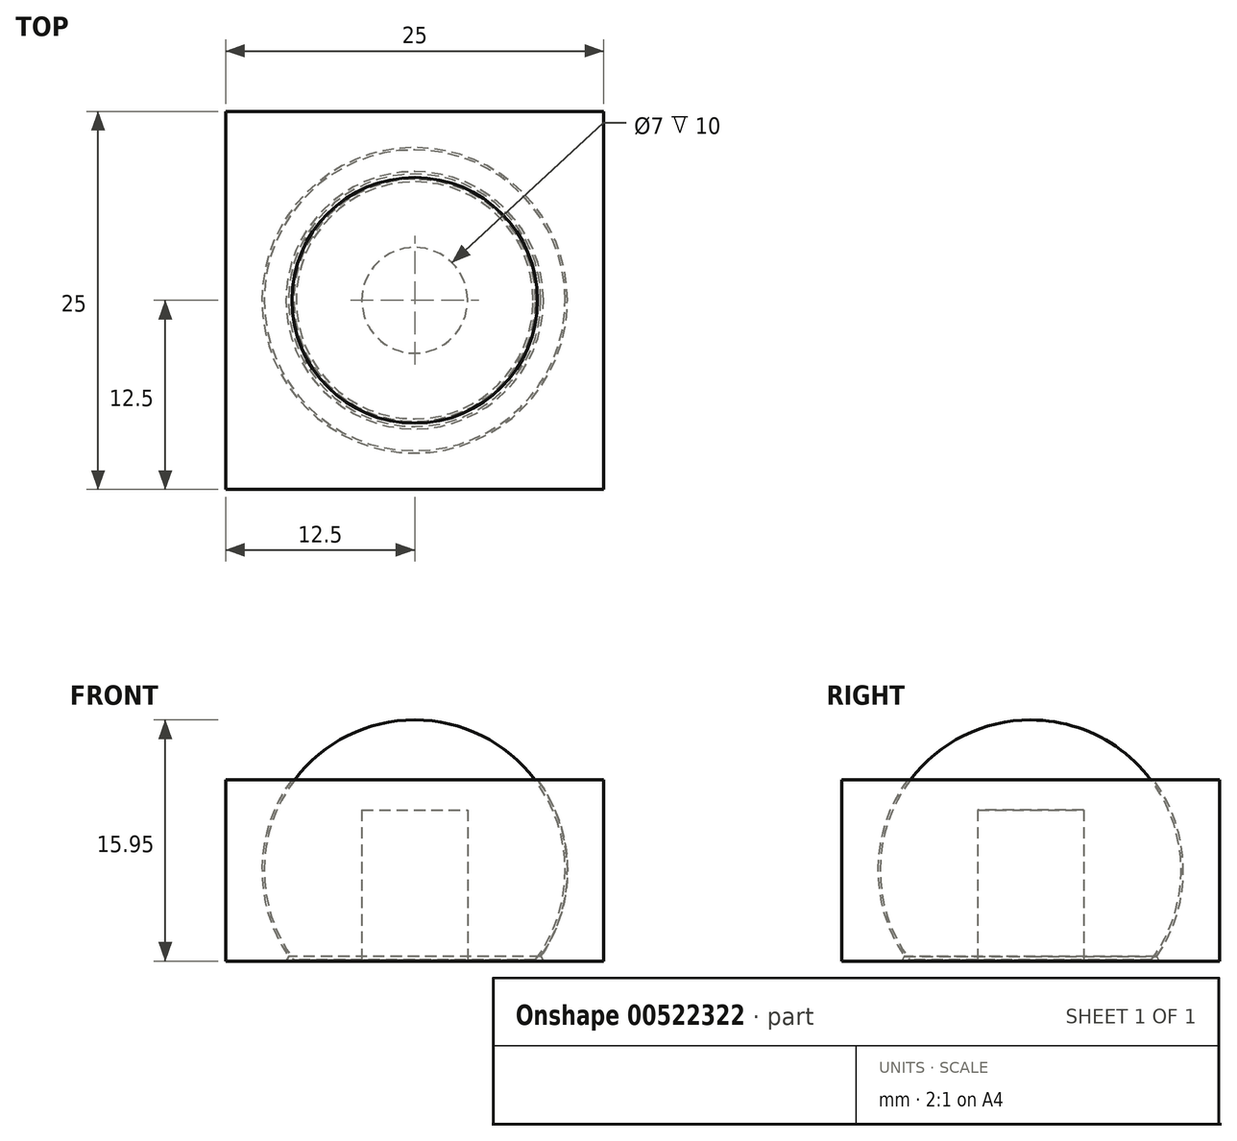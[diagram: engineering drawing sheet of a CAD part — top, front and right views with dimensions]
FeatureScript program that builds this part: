
annotation { "Feature Type Name" : "Feature", "Feature Type Description" : "" }
export const myFeature = defineFeature(function(context is Context, id is Id, definition is map)
    precondition{}
    {
        {
            var Q0;
            Q0=qCreatedBy(makeId("Top.planeOp"),FACE);
            var sketch = newSketch(context, id + "F0", { "sketchPlane" : qUnion([Q0])});
            skLineSegment(sketch, "E0.bottom", {"start": v(-12.5, 12.5) * mm, "end": v(12.5, 12.5) * mm});
            skLineSegment(sketch, "E0.top", {"start": v(-12.5, -12.5) * mm, "end": v(12.5, -12.5) * mm});
            skLineSegment(sketch, "E0.left", {"start": v(-12.5, 12.5) * mm, "end": v(-12.5, -12.5) * mm});
            skLineSegment(sketch, "E0.right", {"start": v(12.5, 12.5) * mm, "end": v(12.5, -12.5) * mm});
            skLineSegment(sketch, "E1", {"start": v(0, -17.22) * mm, "end": v(0, 15.83) * mm, "construction": true});
            skLineSegment(sketch, "E2", {"start": v(-20.04, 0) * mm, "end": v(21, 0) * mm, "construction": true});
            skSolve(sketch);
        }
        {
            var Q0;
            Q0 = qSketchRegion(id + "F0", true);
            extrude(context, id + "F1", {"entities" : qUnion([Q0]), "depth" : 12 * mm, "offsetDistance" : 25 * mm});
        }
        {
            var Q0;
            Q0=qCreatedBy(makeId("Right.planeOp"),FACE);
            var sketch = newSketch(context, id + "F2", { "sketchPlane" : qUnion([Q0])});
            skLineSegment(sketch, "E3.0", {"start": v(12.5, 0) * mm, "end": v(-12.5, 0) * mm, "construction": true});
            skLineSegment(sketch, "E3.1", {"start": v(12.5, 12) * mm, "end": v(-12.5, 12) * mm, "construction": true});
            skLineSegment(sketch, "E4", {"start": v(-21.21, 6) * mm, "end": v(21.87, 6) * mm, "construction": true});
            skArc(sketch, "E5", {"start": v(0, -4.1) * mm, "mid": v(10.1, 6) * mm, "end": v(0, 16.1) * mm});
            skLineSegment(sketch, "E6", {"start": v(0, 16.1) * mm, "end": v(0, -4.1) * mm});
            skSolve(sketch);
        }
        {
            var Q0;
            Q0=makeQuery(id+"F2.imprint","IMPRINT",FACE,{"disambiguationData":[TD([[makeQuery(id+"F2.imprint","IMPRINT",EDGE,{"derivedFrom":sQuery(id+"F2.wireOp",EDGE,"E5")}),1.0]])]});
            var Q1;
            Q1=sQuery(id+"F2.wireOp",EDGE,"E5");
            var Q2;
            Q2=sQuery(id+"F2.wireOp",EDGE,"E6");
            revolve(context, id + "F3", {"operationType" : NewBodyOperationType.REMOVE, "entities" : qUnion([Q0]), "surfaceEntities" : qUnion([Q1]), "axis" : qUnion([Q2]), "revolveType" : RevolveType.FULL, "oppositeDirection" : true});
        }
        {
            var Q0;
            Q0=qCreatedBy(makeId("Right.planeOp"),FACE);
            var sketch = newSketch(context, id + "F4", { "sketchPlane" : qUnion([Q0])});
            skArc(sketch, "E7.0", {"start": v(0, -4.1) * mm, "mid": v(10.1, 6) * mm, "end": v(0, 16.1) * mm, "construction": true});
            skLineSegment(sketch, "E7.1", {"start": v(0, 16.1) * mm, "end": v(0, 0) * mm, "construction": true});
            skArc(sketch, "E8", {"start": v(7.94, 0) * mm, "mid": v(8.9, 10.43) * mm, "end": v(0, 15.95) * mm});
            skLineSegment(sketch, "E9", {"start": v(0, 15.95) * mm, "end": v(0, 0) * mm});
            skLineSegment(sketch, "E10", {"start": v(0, 0) * mm, "end": v(7.94, 0) * mm});
            skLineSegment(sketch, "E11.trimOffspring", {"start": v(0, -3.95) * mm, "end": v(0, -4.1) * mm, "construction": true});
            skSolve(sketch);
        }
        {
            var Q0;
            Q0 = qSketchRegion(id + "F4", true);
            var Q1;
            Q1=sQuery(id+"F4.wireOp",EDGE,"E9");
            revolve(context, id + "F5", {"entities" : qUnion([Q0]), "axis" : qUnion([Q1]), "revolveType" : RevolveType.FULL});
        }
        {
            var Q0;
            Q0=makeQuery(id+"F5.opRevolve","SWEPT_FACE",FACE,{"disambiguationData":[OSD([sQuery(id+"F4.wireOp",EDGE,"E10")])]});
            var sketch = newSketch(context, id + "F6", { "sketchPlane" : qUnion([Q0])});
            skCircle(sketch, "E12", {"center": v(0, 0) * mm, "radius": 3.5 * mm});
            skSolve(sketch);
        }
        {
            var Q0;
            Q0=makeQuery(id+"F6.imprint","IMPRINT",FACE,{"disambiguationData":[TD([[makeQuery(id+"F6.imprint","IMPRINT",EDGE,{"derivedFrom":sQuery(id+"F6.wireOp",EDGE,"E12")}),1.0]])]});
            extrude(context, id + "F7", {"entities" : qUnion([Q0]), "operationType" : NewBodyOperationType.REMOVE, "oppositeDirection" : true, "depth" : 10 * mm, "offsetDistance" : 25 * mm});
        }
        {
            var Q0;
            Q0=makeQuery(id+"F3.boolean.opBoolean","INTERSECT",EDGE,{"derivedFrom":[makeQuery(id+"F1.opExtrude","CAP_FACE",FACE,{"disambiguationData":[OSD([sQuery(id+"F0.wireOp",EDGE,"E0.bottom"),sQuery(id+"F0.wireOp",EDGE,"E0.top"),sQuery(id+"F0.wireOp",EDGE,"E0.left"),sQuery(id+"F0.wireOp",EDGE,"E0.right")])],"isStart":true}),makeQuery(id+"F3.opRevolve","SWEPT_FACE",FACE,{"disambiguationData":[OSD([sQuery(id+"F2.wireOp",EDGE,"E5")])]})]});
            var Q1;
            Q1=makeQuery(id+"F5.opRevolve","SWEPT_EDGE",EDGE,{"disambiguationData":[OSD([sQuery(id+"F4.wireOp",EDGE,"E8"),sQuery(id+"F4.wireOp",EDGE,"E10")])]});
            chamfer(context, id + "F8", {"entities" : qUnion([Q0, Q1]), "width" : 0.2 * mm, "tangentPropagation" : true});
        }
    });
